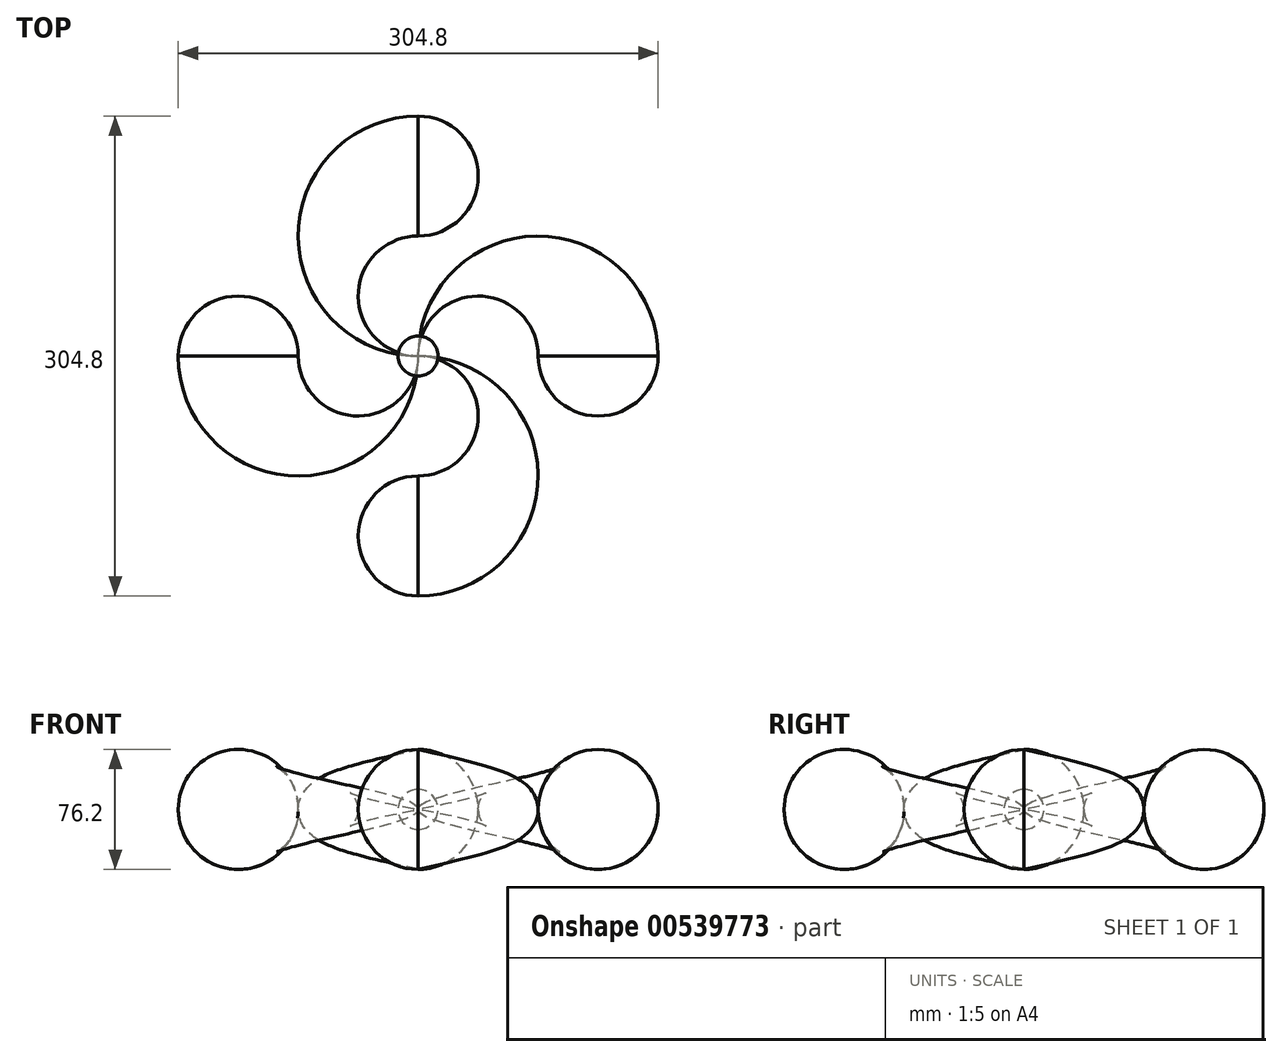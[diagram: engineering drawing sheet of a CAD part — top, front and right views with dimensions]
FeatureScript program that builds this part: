
annotation { "Feature Type Name" : "Feature", "Feature Type Description" : "" }
export const myFeature = defineFeature(function(context is Context, id is Id, definition is map)
    precondition{}
    {
        {
            var Q0;
            Q0=qCreatedBy(makeId("Top.planeOp"),FACE);
            var sketch = newSketch(context, id + "F0", { "sketchPlane" : qUnion([Q0])});
            skCircle(sketch, "E0", {"center": v(38.1, 0) * mm, "radius": 38.1 * mm});
            skCircle(sketch, "E1", {"center": v(114.3, 0) * mm, "radius": 38.1 * mm});
            skCircle(sketch, "E2", {"center": v(76.2, 0) * mm, "radius": 76.2 * mm});
            skSolve(sketch);
        }
        {
            var Q0;
            Q0=qCreatedBy(makeId("Top.planeOp"),FACE);
            var sketch = newSketch(context, id + "F1", { "sketchPlane" : qUnion([Q0])});
            skArc(sketch, "E3.0", {"start": v(152.4, 0) * mm, "mid": v(76.2, 76.2) * mm, "end": v(0, 0) * mm});
            skLineSegment(sketch, "E4", {"start": v(0, 0) * mm, "end": v(152.4, 0) * mm, "construction": true});
            skSolve(sketch);
        }
        {
            var Q0;
            Q0=qCreatedBy(makeId("Top.planeOp"),FACE);
            var sketch = newSketch(context, id + "F2", { "sketchPlane" : qUnion([Q0])});
            skArc(sketch, "E5.0", {"start": v(76.2, 0) * mm, "mid": v(38.1, 38.1) * mm, "end": v(0, 0) * mm});
            skLineSegment(sketch, "E6", {"start": v(0, 0) * mm, "end": v(76.2, 0) * mm, "construction": true});
            skSolve(sketch);
        }
        {
            var Q0;
            Q0=qCreatedBy(makeId("Front.planeOp"),FACE);
            var sketch = newSketch(context, id + "F3", { "sketchPlane" : qUnion([Q0])});
            skArc(sketch, "E7", {"start": v(152.4, 0) * mm, "mid": v(114.3, 38.1) * mm, "end": v(76.2, 0) * mm});
            skLineSegment(sketch, "E8", {"start": v(152.4, 0) * mm, "end": v(76.2, 0) * mm});
            skSolve(sketch);
        }
        {
            var Q0;
            Q0=sQuery(id+"F2.wireOp",EDGE,"E6");
            cPoint(context, id + "F4", {"entities" : qUnion([Q0]), "parameter" : 0.5});
        }
        {
            var Q0;
            Q0=qCreatedBy(makeId("Right.planeOp"),FACE);
            var Q1;
            Q1 = qCreatedBy(id + "F4" ,VERTEX);
            cPlane(context, id + "F5", {"entities" : qUnion([Q0, Q1]), "cplaneType" : CPlaneType.PLANE_POINT, "offset" : 25.4 * mm, "width" : 152.4 * mm, "height" : 152.4 * mm});
        }
        {
            var Q0;
            Q0=qCreatedBy(id+"F5.planeOp",FACE);
            var sketch = newSketch(context, id + "F6", { "sketchPlane" : qUnion([Q0])});
            skLineSegment(sketch, "E9", {"start": v(38.1, 0) * mm, "end": v(66, 0) * mm});
            skArc(sketch, "E10", {"start": v(66, 0) * mm, "mid": v(52.05, 13.95) * mm, "end": v(38.1, 0) * mm});
            skSolve(sketch);
        }
        {
            var Q0;
            Q0=makeQuery(id+"F3.imprint","IMPRINT",FACE,{"disambiguationData":[TD([[makeQuery(id+"F3.imprint","IMPRINT",EDGE,{"derivedFrom":sQuery(id+"F3.wireOp",EDGE,"E7")}),1.0]])]});
            var Q1;
            Q1=makeQuery(id+"F6.imprint","IMPRINT",FACE,{"disambiguationData":[TD([[makeQuery(id+"F6.imprint","IMPRINT",EDGE,{"derivedFrom":sQuery(id+"F6.wireOp",EDGE,"E9")}),1.0]])]});
            var Q2;
            Q2=sQuery(id+"F2.wireOp",VERTEX,"E6.start");
            var Q3;
            Q3=sQuery(id+"F1.wireOp",EDGE,"E3.0");
            var Q4;
            Q4=sQuery(id+"F2.wireOp",EDGE,"E5.0");
            loft(context, id + "F7", {"addGuides" : true, "sheetProfilesArray" : [{ "sheetProfileEntities" : qUnion([Q0]) }, { "sheetProfileEntities" : qUnion([Q1]) }, { "sheetProfileEntities" : qUnion([Q2]) }], "guidesArray" : [{ "guideEntities" : qUnion([Q3]), "guideDerivativeType" : LoftGuideDerivativeType.DEFAULT, "guideDerivativeMagnitude" : 1 }, { "guideEntities" : qUnion([Q4]), "guideDerivativeType" : LoftGuideDerivativeType.DEFAULT, "guideDerivativeMagnitude" : 1 }]});
        }
        {
            var Q0;
            Q0=makeQuery(id+"F7.opLoft","CAP_FACE",FACE,{"disambiguationData":[OSD([makeQuery(id+"F3.imprint","IMPRINT",FACE,{"disambiguationData":[TD([[makeQuery(id+"F3.imprint","IMPRINT",EDGE,{"derivedFrom":sQuery(id+"F3.wireOp",EDGE,"E7")}),1.0]])]})])],"isStart":true});
            var sketch = newSketch(context, id + "F8", { "sketchPlane" : qUnion([Q0])});
            skLineSegment(sketch, "E11", {"start": v(152.4, 0) * mm, "end": v(225.27, 0) * mm, "construction": true});
            skSolve(sketch);
        }
        {
            var Q0;
            {var subQ0=sQuery(id+"F2.wireOp",EDGE,"E5.0");var subQ1=sQuery(id+"F1.wireOp",EDGE,"E3.0");Q0=makeQuery(id+"F8.imprint","IMPRINT",FACE,{"disambiguationData":[TD([[makeQuery(id+"F8.imprint","IMPRINT",EDGE,{"derivedFrom":makeQuery(id+"F7.opLoft","MID_CAP_EDGE",EDGE,{"disambiguationData":[OSD([subQ1,subQ0,sQuery(id+"F3.wireOp",EDGE,"E7")])],"capPos":0.0})}),1.0]])]});}
            var Q1;
            Q1=sQuery(id+"F8.wireOp",EDGE,"E11");
            revolve(context, id + "F9", {"operationType" : NewBodyOperationType.ADD, "entities" : qUnion([Q0]), "axis" : qUnion([Q1]), "revolveType" : RevolveType.ONE_DIRECTION, "angle" : 90 * degree});
        }
        {
            var Q0;
            Q0=makeQuery(id+"F7.opLoft","SWEPT_BODY",BODY,{"disambiguationData":[OSD([sQuery(id+"F1.wireOp",EDGE,"E3.0"),sQuery(id+"F2.wireOp",VERTEX,"E6.start"),sQuery(id+"F2.wireOp",EDGE,"E5.0"),makeQuery(id+"F3.imprint","IMPRINT",FACE,{"disambiguationData":[TD([[makeQuery(id+"F3.imprint","IMPRINT",EDGE,{"derivedFrom":sQuery(id+"F3.wireOp",EDGE,"E7")}),1.0]])]}),sQuery(id+"F6.wireOp",EDGE,"E9")])]});
            var Q1;
            {var subQ0=sQuery(id+"F3.wireOp",EDGE,"E8");var subQ1=sQuery(id+"F2.wireOp",EDGE,"E5.0");var subQ2=sQuery(id+"F1.wireOp",EDGE,"E3.0");Q1=makeQuery(id+"F9.boolean.opBoolean","MERGE",FACE,{"derivedFrom":[makeQuery(id+"F7.opLoft","SWEPT_FACE",FACE,{"disambiguationData":[OSD([subQ2,subQ1,subQ0,sQuery(id+"F6.wireOp",EDGE,"E9"),sQuery(id+"F6.wireOp",EDGE,"E10")])]}),makeQuery(id+"F9.opRevolve","CAP_FACE",FACE,{"disambiguationData":[OSD([subQ2,subQ1,sQuery(id+"F3.wireOp",EDGE,"E7"),subQ0])],"isStart":false})]});}
            mirror(context, id + "F10", {"operationType" : NewBodyOperationType.ADD, "entities" : qUnion([Q0]), "mirrorPlane" : qUnion([Q1])});
        }
        {
            var Q0;
            Q0=qCreatedBy(makeId("Front.planeOp"),FACE);
            var sketch = newSketch(context, id + "F11", { "sketchPlane" : qUnion([Q0])});
            skLineSegment(sketch, "E12", {"start": v(0, 0) * mm, "end": v(0, 122.3) * mm, "construction": true});
            skSolve(sketch);
        }
        {
            var Q0;
            Q0=makeQuery(id+"F7.opLoft","SWEPT_BODY",BODY,{"disambiguationData":[OSD([sQuery(id+"F1.wireOp",EDGE,"E3.0"),sQuery(id+"F2.wireOp",VERTEX,"E6.start"),sQuery(id+"F2.wireOp",EDGE,"E5.0"),makeQuery(id+"F3.imprint","IMPRINT",FACE,{"disambiguationData":[TD([[makeQuery(id+"F3.imprint","IMPRINT",EDGE,{"derivedFrom":sQuery(id+"F3.wireOp",EDGE,"E7")}),1.0]])]}),sQuery(id+"F6.wireOp",EDGE,"E9")])]});
            var Q1;
            Q1=sQuery(id+"F11.wireOp",EDGE,"E12");
            circularPattern(context, id + "F12", {"entities" : qUnion([Q0]), "axis" : qUnion([Q1]), "angle" : 360 * degree, "instanceCount" : 4, "equalSpace" : true});
        }
        {
            var Q0;
            Q0=qCreatedBy(makeId("Front.planeOp"),FACE);
            var sketch = newSketch(context, id + "F13", { "sketchPlane" : qUnion([Q0])});
            skArc(sketch, "E13", {"start": v(0, 12.7) * mm, "mid": v(-12.7, 0) * mm, "end": v(0, -12.7) * mm});
            skLineSegment(sketch, "E14", {"start": v(0, -12.7) * mm, "end": v(0, 12.7) * mm});
            skSolve(sketch);
        }
        {
            var Q0;
            Q0=qCreatedBy(makeId("Front.planeOp"),FACE);
            var sketch = newSketch(context, id + "F14", { "sketchPlane" : qUnion([Q0])});
            skLineSegment(sketch, "E15", {"start": v(0, 0) * mm, "end": v(0, 39.26) * mm, "construction": true});
            skSolve(sketch);
        }
        {
            var Q0;
            Q0=makeQuery(id+"F13.imprint","IMPRINT",FACE,{"disambiguationData":[TD([[makeQuery(id+"F13.imprint","IMPRINT",EDGE,{"derivedFrom":sQuery(id+"F13.wireOp",EDGE,"E13")}),1.0]])]});
            var Q1;
            Q1=sQuery(id+"F14.wireOp",EDGE,"E15");
            revolve(context, id + "F15", {"entities" : qUnion([Q0]), "axis" : qUnion([Q1]), "revolveType" : RevolveType.FULL});
        }
    });
